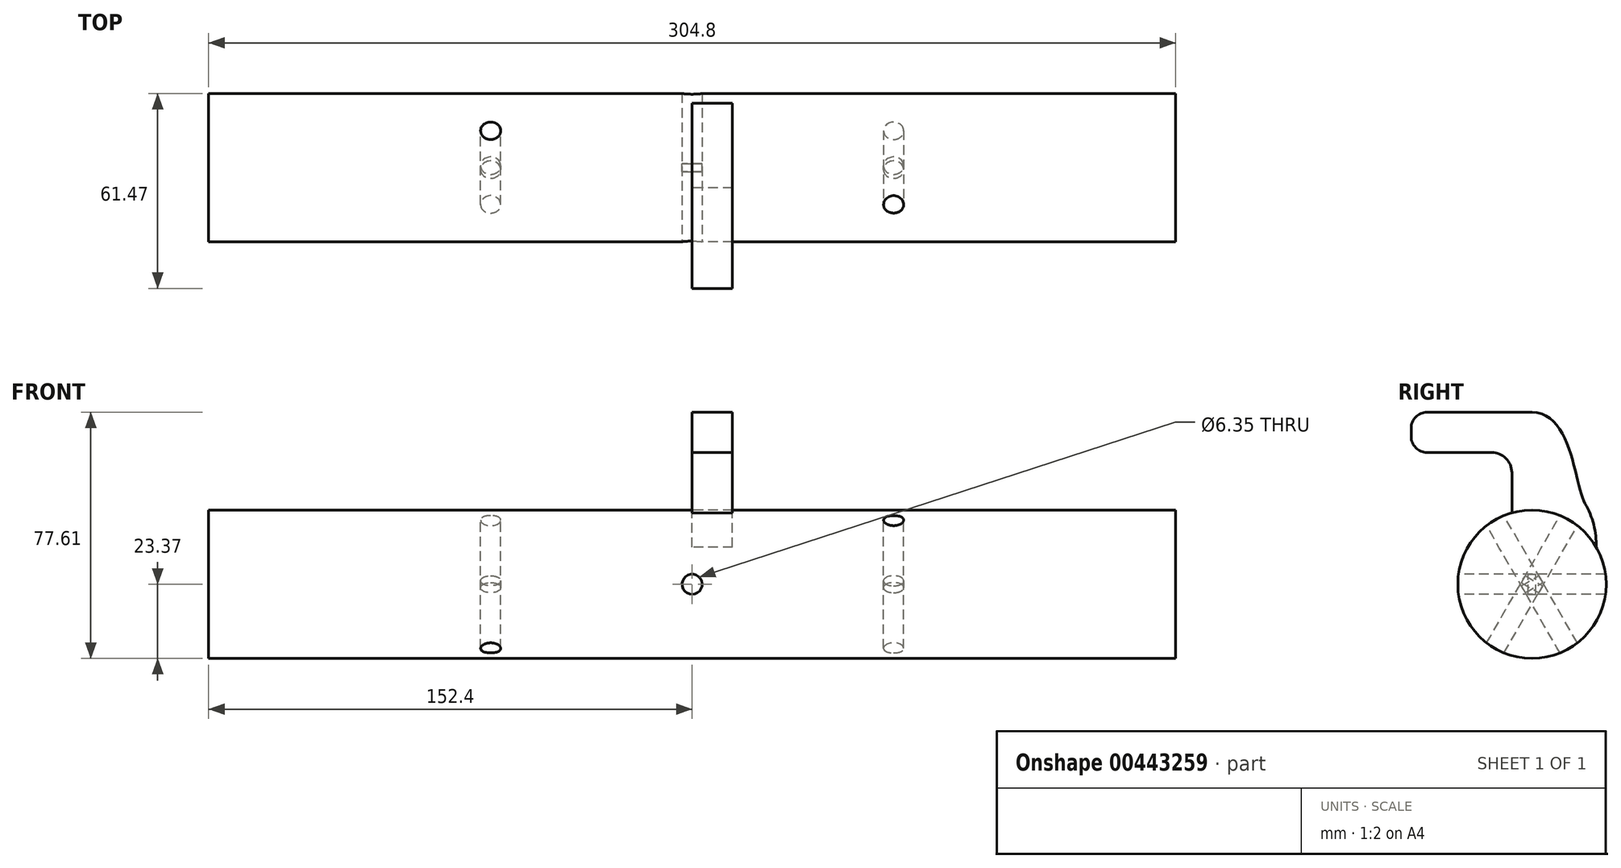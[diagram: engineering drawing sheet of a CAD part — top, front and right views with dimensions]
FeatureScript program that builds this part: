
annotation { "Feature Type Name" : "Feature", "Feature Type Description" : "" }
export const myFeature = defineFeature(function(context is Context, id is Id, definition is map)
    precondition{}
    {
        {
            assignVariable(context, id + "F0", {"name" : "hook", "anyValue" : 2.5});
        }
        {
            var Q0;
            Q0=qCreatedBy(makeId("Right.planeOp"),FACE);
            var sketch = newSketch(context, id + "F1", { "sketchPlane" : qUnion([Q0])});
            skCircle(sketch, "E0", {"center": v(0, 0) * mm, "radius": 23.37 * mm});
            skSolve(sketch);
        }
        {
            var Q0;
            Q0=sQuery(id+"F1.wireOp",EDGE,"E0");
            cPlane(context, id + "F2", {"entities" : qUnion([Q0]), "cplaneType" : CPlaneType.LINE_ANGLE, "offset" : 25.4 * mm, "angle" : 60 * degree, "width" : 152.4 * mm, "height" : 152.4 * mm});
        }
        {
            var Q0;
            Q0=sQuery(id+"F1.wireOp",EDGE,"E0");
            cPlane(context, id + "F3", {"entities" : qUnion([Q0]), "cplaneType" : CPlaneType.LINE_ANGLE, "offset" : 25.4 * mm, "angle" : 120 * degree, "width" : 152.4 * mm, "height" : 152.4 * mm});
        }
        {
            var Q0;
            Q0=makeQuery(id+"F1.imprint","IMPRINT",FACE,{"disambiguationData":[TD([[makeQuery(id+"F1.imprint","IMPRINT",EDGE,{"derivedFrom":sQuery(id+"F1.wireOp",EDGE,"E0")}),1.0]])]});
            extrude(context, id + "F4", {"entities" : qUnion([Q0]), "depth" : 304.8 * mm, "symmetric" : true});
        }
        {
            var Q0;
            Q0=qCreatedBy(makeId("Front.planeOp"),FACE);
            var sketch = newSketch(context, id + "F5", { "sketchPlane" : qUnion([Q0])});
            skCircle(sketch, "E1", {"center": v(0, 0) * mm, "radius": 3.18 * mm});
            skSolve(sketch);
        }
        {
            var Q0;
            Q0=qCreatedBy(id+"F2.planeOp",FACE);
            var sketch = newSketch(context, id + "F6", { "sketchPlane" : qUnion([Q0])});
            skCircle(sketch, "E2", {"center": v(-63.5, 0) * mm, "radius": 3.18 * mm});
            skSolve(sketch);
        }
        {
            var Q0;
            Q0=qCreatedBy(id+"F3.planeOp",FACE);
            var sketch = newSketch(context, id + "F7", { "sketchPlane" : qUnion([Q0])});
            skCircle(sketch, "E3", {"center": v(63.5, 0) * mm, "radius": 3.18 * mm});
            skSolve(sketch);
        }
        {
            var Q0;
            Q0=makeQuery(id+"F5.imprint","IMPRINT",FACE,{"disambiguationData":[TD([[makeQuery(id+"F5.imprint","IMPRINT",EDGE,{"derivedFrom":sQuery(id+"F5.wireOp",EDGE,"E1")}),1.0]])]});
            extrude(context, id + "F8", {"entities" : qUnion([Q0]), "operationType" : NewBodyOperationType.REMOVE, "oppositeDirection" : true, "depth" : 50.8 * mm, "symmetric" : true});
        }
        {
            var Q0;
            Q0=makeQuery(id+"F7.imprint","IMPRINT",FACE,{"disambiguationData":[TD([[makeQuery(id+"F7.imprint","IMPRINT",EDGE,{"derivedFrom":sQuery(id+"F7.wireOp",EDGE,"E3")}),1.0]])]});
            extrude(context, id + "F9", {"entities" : qUnion([Q0]), "operationType" : NewBodyOperationType.REMOVE, "oppositeDirection" : true, "depth" : 50.8 * mm, "symmetric" : true});
        }
        {
            var Q0;
            Q0=makeQuery(id+"F6.imprint","IMPRINT",FACE,{"disambiguationData":[TD([[makeQuery(id+"F6.imprint","IMPRINT",EDGE,{"derivedFrom":sQuery(id+"F6.wireOp",EDGE,"E2")}),1.0]])]});
            extrude(context, id + "F10", {"entities" : qUnion([Q0]), "operationType" : NewBodyOperationType.REMOVE, "oppositeDirection" : true, "depth" : 50.8 * mm, "symmetric" : true});
        }
        {
            var Q0;
            Q0=makeQuery(id+"F6.imprint","IMPRINT",FACE,{"disambiguationData":[TD([[makeQuery(id+"F6.imprint","IMPRINT",EDGE,{"derivedFrom":sQuery(id+"F6.wireOp",EDGE,"E2")}),1.0]])]});
            extrude(context, id + "F11", {"entities" : qUnion([Q0]), "depth" : (getVariable(context, 'hook')) * mm, "symmetric" : true});
        }
        {
            var Q0;
            Q0=makeQuery(id+"F5.imprint","IMPRINT",FACE,{"disambiguationData":[TD([[makeQuery(id+"F5.imprint","IMPRINT",EDGE,{"derivedFrom":sQuery(id+"F5.wireOp",EDGE,"E1")}),1.0]])]});
            extrude(context, id + "F12", {"entities" : qUnion([Q0]), "depth" : (getVariable(context, 'hook')) * mm, "symmetric" : true});
        }
        {
            var Q0;
            Q0=makeQuery(id+"F7.imprint","IMPRINT",FACE,{"disambiguationData":[TD([[makeQuery(id+"F7.imprint","IMPRINT",EDGE,{"derivedFrom":sQuery(id+"F7.wireOp",EDGE,"E3")}),1.0]])]});
            var Q1;
            Q1=sQuery(id+"F7.wireOp",EDGE,"E3");
            extrude(context, id + "F13", {"entities" : qUnion([Q0]), "surfaceEntities" : qUnion([Q1]), "depth" : (getVariable(context, 'hook')) * mm, "symmetric" : true});
        }
        {
            var Q0;
            Q0=qCreatedBy(makeId("Right.planeOp"),FACE);
            var sketch = newSketch(context, id + "F14", { "sketchPlane" : qUnion([Q0])});
            skCircle(sketch, "E4.0", {"center": v(0, 0) * mm, "radius": 23.37 * mm});
            skLineSegment(sketch, "E5", {"start": v(-6.35, 22.49) * mm, "end": v(-6.35, 35.19) * mm});
            skLineSegment(sketch, "E6", {"start": v(-12.7, 41.54) * mm, "end": v(-38.1, 41.54) * mm});
            skLineSegment(sketch, "E7", {"start": v(-38.1, 41.54) * mm, "end": v(-38.1, 54.24) * mm});
            skLineSegment(sketch, "E8", {"start": v(-38.1, 54.24) * mm, "end": v(0, 54.24) * mm});
            skLineSegment(sketch, "E9", {"start": v(6.35, 35.19) * mm, "end": v(6.35, 22.49) * mm});
            skArc(sketch, "E10", {"start": v(20.24, 11.68) * mm, "mid": v(16.72, 25.46) * mm, "end": v(6.35, 35.19) * mm});
            skLineSegment(sketch, "E11", {"start": v(0, 0) * mm, "end": v(16.9, 0) * mm, "construction": true});
            skLineSegment(sketch, "E12", {"start": v(20.24, 11.68) * mm, "end": v(0, 0) * mm, "construction": true});
            skPoint(sketch, "E13.visualSharp", {"position": v(-6.35, 41.54) * mm});
            skArc(sketch, "E13.filletArc", {"start": v(-6.35, 35.19) * mm, "mid": v(-8.2, 39.68) * mm, "end": v(-12.7, 41.54) * mm});
            skFitSpline(sketch, "E14", {"points": [v(0, 54.24) * mm, v(16.72, 25.46) * mm], "startDerivative": vector(38.1, 0) * mm, "endDerivative": vector(9.7, -16.4) * mm});
            skLineSegment(sketch, "E15", {"start": v(13.49, 30.93) * mm, "end": v(16.72, 25.46) * mm, "construction": true});
            skSolve(sketch);
        }
        {
            var Q0;
            {var subQ0=sQuery(id+"F14.wireOp",EDGE,"E14");Q0=makeQuery(id+"F14.imprint","IMPRINT",FACE,{"disambiguationData":[TD([[makeQuery(id+"F14.imprint","IMPRINT",EDGE,{"derivedFrom":subQ0}),-1.0]])]});}
            var Q1;
            {var subQ0=sQuery(id+"F14.wireOp",EDGE,"E9");var subQ1=sQuery(id+"F14.wireOp",EDGE,"E4.0");var subQ2=makeQuery(id+"F14.imprint","INTERSECT",VERTEX,{"derivedFrom":[subQ1,subQ0]});Q1=makeQuery(id+"F14.imprint","IMPRINT",FACE,{"disambiguationData":[TD([[makeQuery(id+"F14.imprint","IMPRINT",EDGE,{"disambiguationData":[TD([[subQ2,1.0]])],"derivedFrom":subQ1}),-1.0]])]});}
            var Q2;
            {var subQ0=sQuery(id+"F14.wireOp",EDGE,"E5");Q2=makeQuery(id+"F14.imprint","IMPRINT",FACE,{"disambiguationData":[TD([[makeQuery(id+"F14.imprint","IMPRINT",EDGE,{"derivedFrom":subQ0}),-1.0]])]});}
            extrude(context, id + "F15", {"entities" : qUnion([Q0, Q1, Q2]), "depth" : 12.7 * mm});
        }
        {
            var Q0;
            Q0=makeQuery(id+"F15.opExtrude","SWEPT_EDGE",EDGE,{"disambiguationData":[OSD([sQuery(id+"F14.wireOp",EDGE,"E7"),sQuery(id+"F14.wireOp",EDGE,"E8")])]});
            var Q1;
            Q1=makeQuery(id+"F15.opExtrude","SWEPT_EDGE",EDGE,{"disambiguationData":[OSD([sQuery(id+"F14.wireOp",EDGE,"E6"),sQuery(id+"F14.wireOp",EDGE,"E7")])]});
            fillet(context, id + "F16", {"entities" : qUnion([Q0, Q1]), "radius" : 5.08 * mm, "tangentPropagation" : true, "allowEdgeOverflow" : false});
        }
    });
